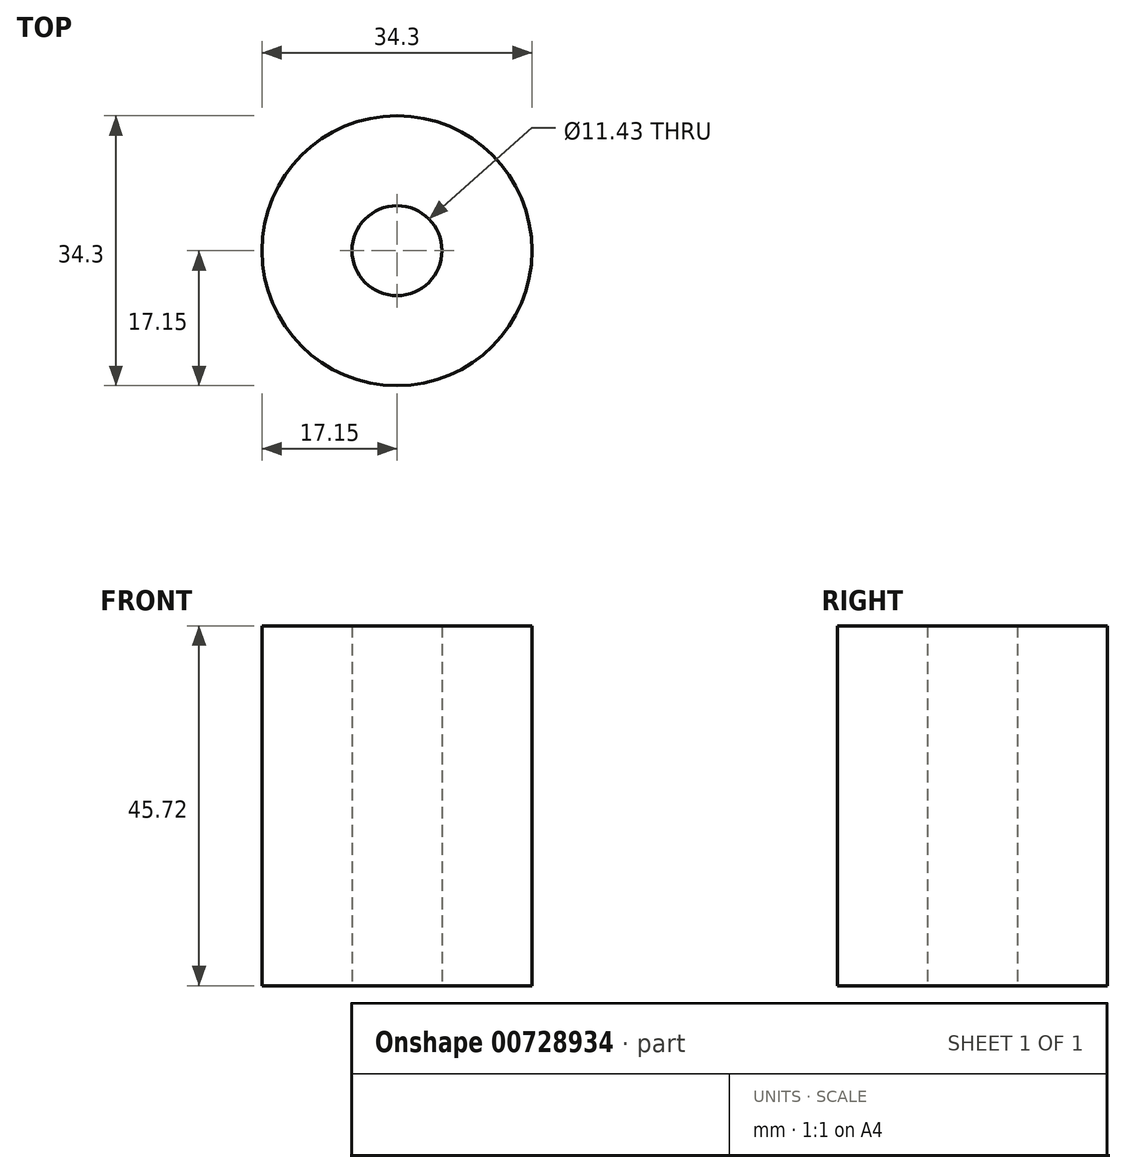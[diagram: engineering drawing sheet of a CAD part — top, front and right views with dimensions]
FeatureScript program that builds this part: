
annotation { "Feature Type Name" : "Feature", "Feature Type Description" : "" }
export const myFeature = defineFeature(function(context is Context, id is Id, definition is map)
    precondition{}
    {
        {
            var Q0;
            Q0=qCreatedBy(makeId("Top.planeOp"),FACE);
            var sketch = newSketch(context, id + "F0", { "sketchPlane" : qUnion([Q0])});
            skCircle(sketch, "E0", {"center": v(0, 0) * mm, "radius": 5.71 * mm});
            skCircle(sketch, "E1", {"center": v(0, 0) * mm, "radius": 17.14 * mm});
            skSolve(sketch);
        }
        {
            var Q0;
            Q0 = qSketchRegion(id + "F0", true);
            extrude(context, id + "F1", {"entities" : qUnion([Q0]), "depth" : 45.72 * mm, "offsetDistance" : 25 * mm});
        }
    });
